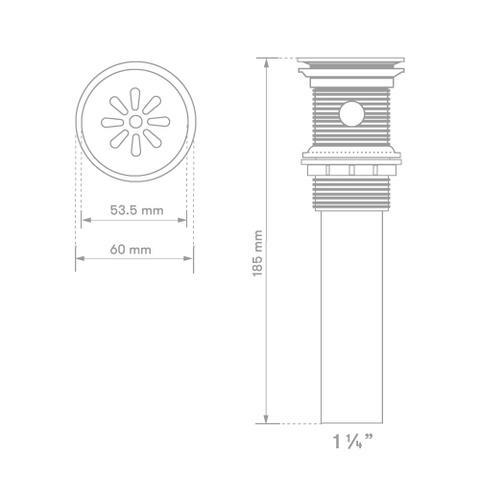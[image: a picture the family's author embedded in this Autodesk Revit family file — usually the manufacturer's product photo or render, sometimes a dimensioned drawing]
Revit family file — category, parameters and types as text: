
# Revit family: 01-3211-11 DESAGÜE PUSH CORTO CON REBOSE
name_source: partatom
category: Aparatos sanitarios
units: mm (PartAtom-declared; Revit-internal decimal feet)

## family parameters
Compartido = No
Corte con vacíos al cargar = No
Cota de conector redondo = Diámetro de uso
Número OmniClass = 23.45.00.00
Punto de cálculo de habitación = No
Se basa en plano de trabajo = No
Siempre vertical = Sí
Tipo de pieza = Normal
Título OmniClass = Sanitary, Laundry, and Cleaning Equipment

## types (1)
- 01-3211-11 DESAGÜE PUSH CORTO CON REBOSE
    Caucho = Caucho
    Conexión AC = No
    Conexión AF = No
    Conexión de residuos = No
    Conexión de ventilación = No
    Costo = 0 $
    Elevación por defecto = 0 mm  [stored 0 ft]
    Metal Laton Cromado = Metal Laton Cromado
    Nominal height = 130
    Nominal width = 370
    Plastico - ABS Cromado = Plastico - ABS Cromado
    Weight Net (Kg) = 6.60Kg

note: [stored X ft] marks values corroborated as IEEE doubles in the binary element streams (Revit-internal decimal feet)

## geometry (parser evidence)
native form markers: Blend x2, Sweep x1
no freeform markers — native parametric forms only
